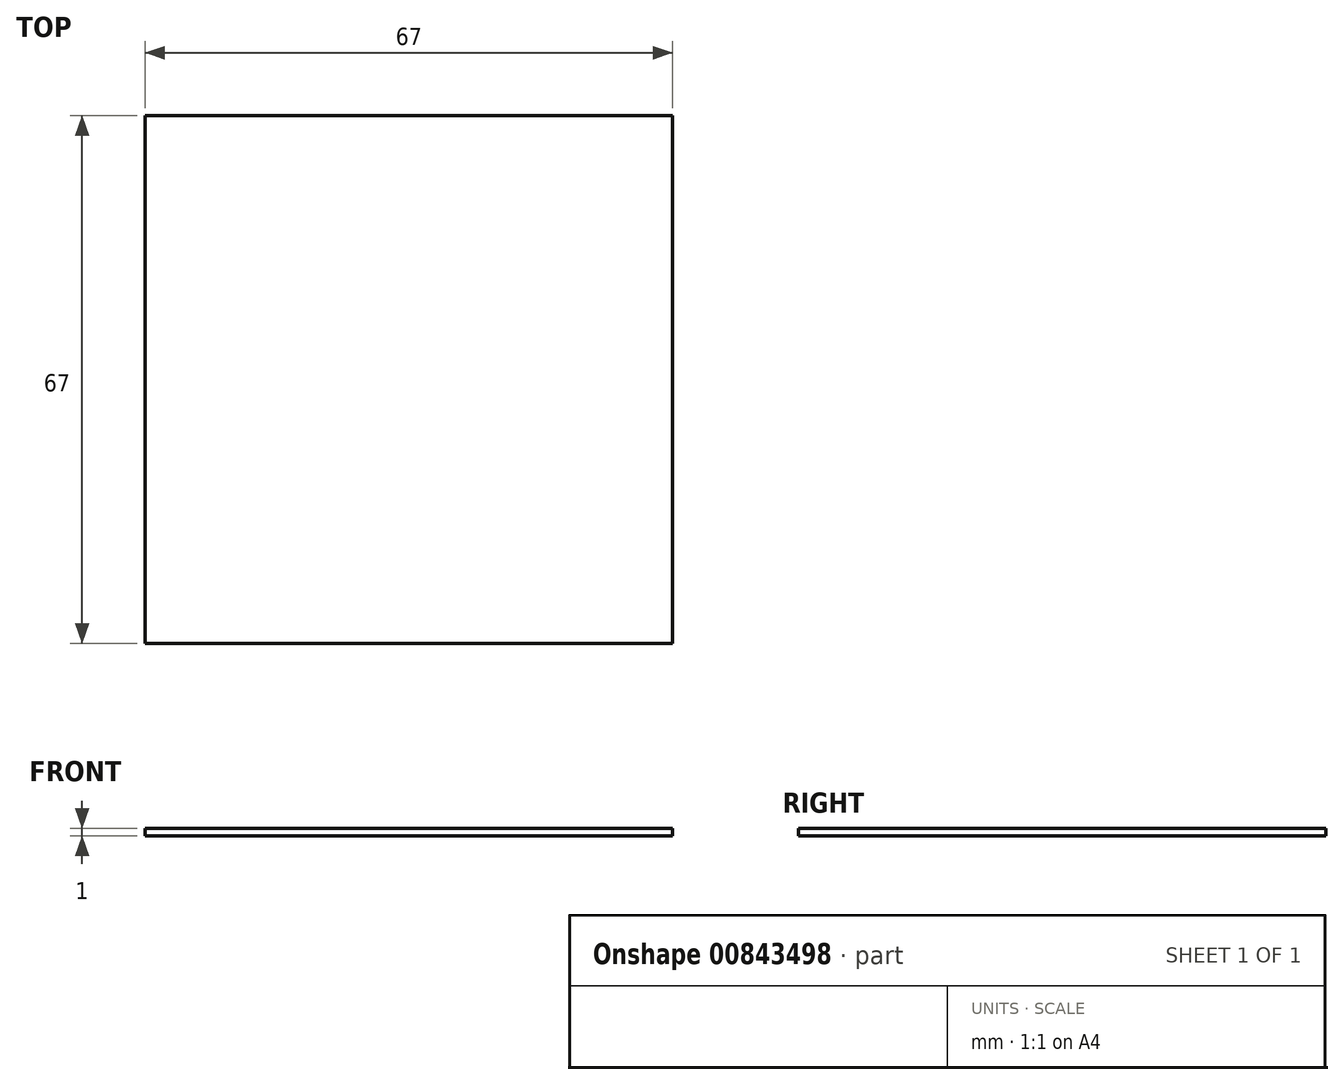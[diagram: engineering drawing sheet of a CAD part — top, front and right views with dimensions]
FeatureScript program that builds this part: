
annotation { "Feature Type Name" : "Feature", "Feature Type Description" : "" }
export const myFeature = defineFeature(function(context is Context, id is Id, definition is map)
    precondition{}
    {
        {
            var Q0;
            Q0=qCreatedBy(makeId("Top.planeOp"),FACE);
            var sketch = newSketch(context, id + "F0", { "sketchPlane" : qUnion([Q0])});
            skLineSegment(sketch, "E0.bottom", {"start": v(-32.43, 28.97) * mm, "end": v(34.57, 28.97) * mm});
            skLineSegment(sketch, "E0.top", {"start": v(-32.43, -38.03) * mm, "end": v(34.57, -38.03) * mm});
            skLineSegment(sketch, "E0.left", {"start": v(-32.43, 28.97) * mm, "end": v(-32.43, -38.03) * mm});
            skLineSegment(sketch, "E0.right", {"start": v(34.57, 28.97) * mm, "end": v(34.57, -38.03) * mm});
            skSolve(sketch);
        }
        {
            var Q0;
            Q0 = qSketchRegion(id + "F0", true);
            extrude(context, id + "F1", {"entities" : qUnion([Q0]), "depth" : 1 * mm, "offsetDistance" : 25 * mm});
        }
    });
